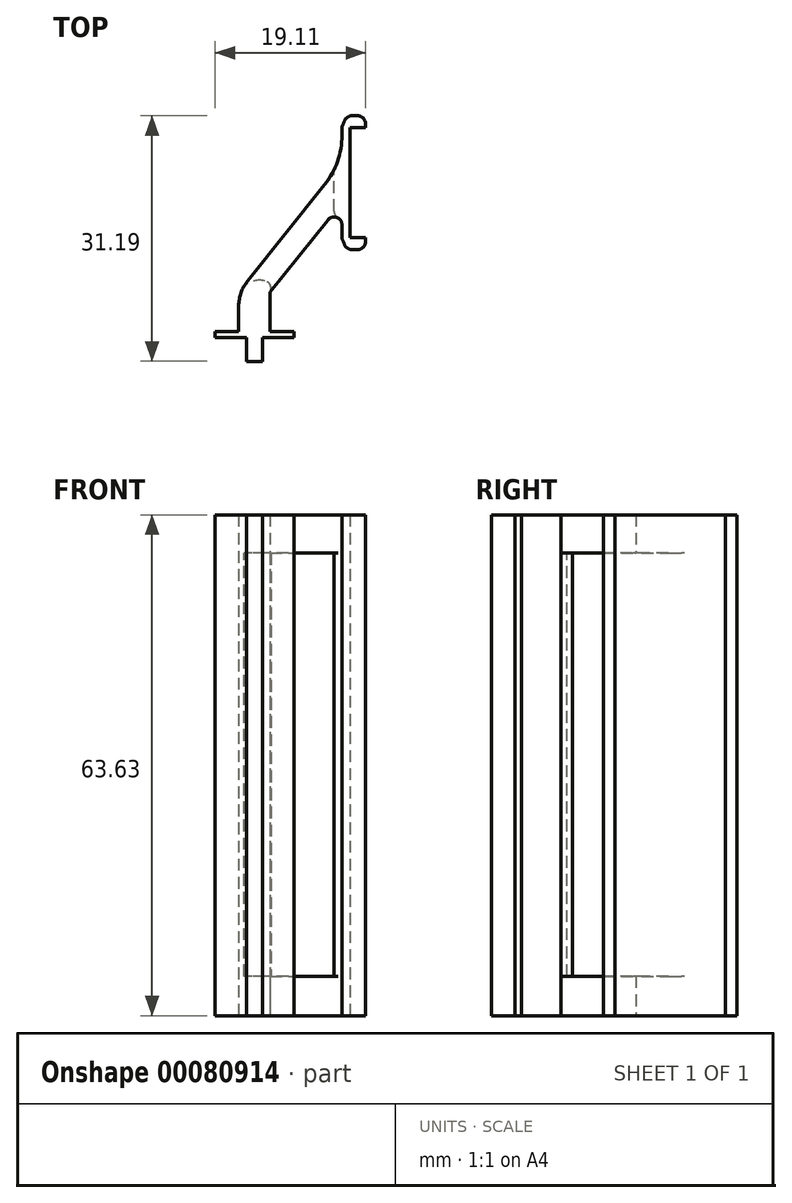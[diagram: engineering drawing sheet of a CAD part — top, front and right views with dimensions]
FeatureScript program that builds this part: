
annotation { "Feature Type Name" : "Feature", "Feature Type Description" : "" }
export const myFeature = defineFeature(function(context is Context, id is Id, definition is map)
    precondition{}
    {
        {
            var Q0;
            Q0=qCreatedBy(makeId("Top.planeOp"),FACE);
            var sketch = newSketch(context, id + "F0", { "sketchPlane" : qUnion([Q0])});
            skLineSegment(sketch, "E0.bottom", {"start": v(-4.08, -12.53) * mm, "end": v(-8.08, -12.53) * mm});
            skLineSegment(sketch, "E0.top", {"start": v(-4.08, -7.53) * mm, "end": v(-8.08, -7.53) * mm});
            skLineSegment(sketch, "E0.left", {"start": v(-4.08, -12.53) * mm, "end": v(-4.08, -7.53) * mm});
            skLineSegment(sketch, "E0.right", {"start": v(-8.08, -12.53) * mm, "end": v(-8.08, -7.53) * mm});
            skPoint(sketch, "E0.middle", {"position": v(-6.08, -10.03) * mm});
            skLineSegment(sketch, "E1", {"start": v(5.03, 8.86) * mm, "end": v(-8.08, -7.53) * mm});
            skLineSegment(sketch, "E2", {"start": v(5.03, 8.86) * mm, "end": v(5.03, 3.86) * mm});
            skLineSegment(sketch, "E3", {"start": v(-4.08, -7.53) * mm, "end": v(5.03, 3.86) * mm});
            skLineSegment(sketch, "E4.bottom", {"start": v(6.03, -1.14) * mm, "end": v(5.03, -1.14) * mm});
            skLineSegment(sketch, "E4.top", {"start": v(6.03, 13.86) * mm, "end": v(5.03, 13.86) * mm});
            skLineSegment(sketch, "E4.left", {"start": v(6.03, -1.14) * mm, "end": v(6.03, 13.86) * mm});
            skLineSegment(sketch, "E4.right", {"start": v(5.03, -1.14) * mm, "end": v(5.03, 13.86) * mm});
            skPoint(sketch, "E4.middle", {"position": v(5.53, 6.36) * mm});
            skLineSegment(sketch, "E5", {"start": v(5.03, 6.36) * mm, "end": v(12.44, 6.36) * mm});
            skLineSegment(sketch, "E6.bottom", {"start": v(6.03, -1.14) * mm, "end": v(8.03, -1.14) * mm});
            skLineSegment(sketch, "E6.top", {"start": v(6.03, -0.64) * mm, "end": v(8.03, -0.64) * mm});
            skLineSegment(sketch, "E6.left", {"start": v(6.03, -1.14) * mm, "end": v(6.03, -0.64) * mm});
            skLineSegment(sketch, "E6.right", {"start": v(8.03, -1.14) * mm, "end": v(8.03, -0.64) * mm});
            skLineSegment(sketch, "E7.bottom", {"start": v(6.03, 13.86) * mm, "end": v(8.03, 13.86) * mm});
            skLineSegment(sketch, "E7.top", {"start": v(6.03, 13.36) * mm, "end": v(8.03, 13.36) * mm});
            skLineSegment(sketch, "E7.left", {"start": v(6.03, 13.86) * mm, "end": v(6.03, 13.36) * mm});
            skLineSegment(sketch, "E7.right", {"start": v(8.03, 13.86) * mm, "end": v(8.03, 13.36) * mm});
            skLineSegment(sketch, "E8.bottom", {"start": v(8.03, 13.36) * mm, "end": v(7.03, 13.36) * mm});
            skLineSegment(sketch, "E8.top", {"start": v(8.03, 10.86) * mm, "end": v(7.03, 10.86) * mm});
            skLineSegment(sketch, "E8.left", {"start": v(8.03, 13.36) * mm, "end": v(8.03, 10.86) * mm});
            skLineSegment(sketch, "E8.right", {"start": v(7.03, 13.36) * mm, "end": v(7.03, 10.86) * mm});
            skLineSegment(sketch, "E9.bottom", {"start": v(8.03, -0.64) * mm, "end": v(7.03, -0.64) * mm});
            skLineSegment(sketch, "E9.top", {"start": v(8.03, 1.86) * mm, "end": v(7.03, 1.86) * mm});
            skLineSegment(sketch, "E9.left", {"start": v(8.03, -0.64) * mm, "end": v(8.03, 1.86) * mm});
            skLineSegment(sketch, "E9.right", {"start": v(7.03, -0.64) * mm, "end": v(7.03, 1.86) * mm});
            skLineSegment(sketch, "E10", {"start": v(-6.08, -10.03) * mm, "end": v(-6.08, -14.83) * mm});
            skLineSegment(sketch, "E11.bottom", {"start": v(-1.08, -13.33) * mm, "end": v(-11.08, -13.33) * mm});
            skLineSegment(sketch, "E11.top", {"start": v(-1.08, -12.53) * mm, "end": v(-11.08, -12.53) * mm});
            skLineSegment(sketch, "E11.left", {"start": v(-1.08, -13.33) * mm, "end": v(-1.08, -12.53) * mm});
            skLineSegment(sketch, "E11.right", {"start": v(-11.08, -13.33) * mm, "end": v(-11.08, -12.53) * mm});
            skPoint(sketch, "E11.middle", {"position": v(-6.08, -12.93) * mm});
            skLineSegment(sketch, "E12.bottom", {"start": v(-5.08, -16.33) * mm, "end": v(-7.08, -16.33) * mm});
            skLineSegment(sketch, "E12.top", {"start": v(-5.08, -13.33) * mm, "end": v(-7.08, -13.33) * mm});
            skLineSegment(sketch, "E12.left", {"start": v(-5.08, -16.33) * mm, "end": v(-5.08, -13.33) * mm});
            skLineSegment(sketch, "E12.right", {"start": v(-7.08, -16.33) * mm, "end": v(-7.08, -13.33) * mm});
            skPoint(sketch, "E12.middle", {"position": v(-6.08, -14.83) * mm});
            skLineSegment(sketch, "E13", {"start": v(4.1, 2.69) * mm, "end": v(4.1, 7.69) * mm});
            skLineSegment(sketch, "E14", {"start": v(-3.15, -6.36) * mm, "end": v(-3.15, -1.36) * mm});
            skSolve(sketch);
        }
        {
            var Q0;
            Q0=makeQuery(id+"F0.imprint","IMPRINT",FACE,{"disambiguationData":[TD([[makeQuery(id+"F0.imprint","IMPRINT",EDGE,{"derivedFrom":sQuery(id+"F0.wireOp",EDGE,"E0.top")}),1.0]])]});
            var Q1;
            {var subQ0=sQuery(id+"F0.wireOp",EDGE,"E0.top");Q1=makeQuery(id+"F0.imprint","IMPRINT",FACE,{"disambiguationData":[TD([[makeQuery(id+"F0.imprint","IMPRINT",EDGE,{"derivedFrom":subQ0}),-1.0]])]});}
            var Q2;
            {var subQ0=sQuery(id+"F0.wireOp",EDGE,"E13");Q2=makeQuery(id+"F0.imprint","IMPRINT",FACE,{"disambiguationData":[TD([[makeQuery(id+"F0.imprint","IMPRINT",EDGE,{"derivedFrom":subQ0}),1.0]])]});}
            var Q3;
            {var subQ6=sQuery(id+"F0.wireOp",EDGE,"E13");Q3=makeQuery(id+"F0.imprint","IMPRINT",FACE,{"disambiguationData":[TD([[makeQuery(id+"F0.imprint","IMPRINT",EDGE,{"derivedFrom":subQ6}),-1.0]])]});}
            var Q4;
            {var subQ4=sQuery(id+"F0.wireOp",EDGE,"E4.bottom");Q4=makeQuery(id+"F0.imprint","IMPRINT",FACE,{"disambiguationData":[TD([[makeQuery(id+"F0.imprint","IMPRINT",EDGE,{"derivedFrom":subQ4}),-1.0]])]});}
            var Q5;
            {var subQ2=sQuery(id+"F0.wireOp",EDGE,"E4.top");Q5=makeQuery(id+"F0.imprint","IMPRINT",FACE,{"disambiguationData":[TD([[makeQuery(id+"F0.imprint","IMPRINT",EDGE,{"derivedFrom":subQ2}),1.0]])]});}
            var Q6;
            Q6=makeQuery(id+"F0.imprint","IMPRINT",FACE,{"disambiguationData":[TD([[makeQuery(id+"F0.imprint","IMPRINT",EDGE,{"derivedFrom":sQuery(id+"F0.wireOp",EDGE,"E8.bottom")}),1.0]])]});
            var Q7;
            Q7=makeQuery(id+"F0.imprint","IMPRINT",FACE,{"disambiguationData":[TD([[makeQuery(id+"F0.imprint","IMPRINT",EDGE,{"derivedFrom":sQuery(id+"F0.wireOp",EDGE,"E7.bottom")}),-1.0]])]});
            var Q8;
            Q8=makeQuery(id+"F0.imprint","IMPRINT",FACE,{"disambiguationData":[TD([[makeQuery(id+"F0.imprint","IMPRINT",EDGE,{"derivedFrom":sQuery(id+"F0.wireOp",EDGE,"E9.bottom")}),-1.0]])]});
            var Q9;
            Q9=makeQuery(id+"F0.imprint","IMPRINT",FACE,{"disambiguationData":[TD([[makeQuery(id+"F0.imprint","IMPRINT",EDGE,{"derivedFrom":sQuery(id+"F0.wireOp",EDGE,"E6.bottom")}),1.0]])]});
            var Q10;
            {var subQ4=sQuery(id+"F0.wireOp",EDGE,"E11.left");Q10=makeQuery(id+"F0.imprint","IMPRINT",FACE,{"disambiguationData":[TD([[makeQuery(id+"F0.imprint","IMPRINT",EDGE,{"derivedFrom":subQ4}),1.0]])]});}
            var Q11;
            {var subQ2=sQuery(id+"F0.wireOp",EDGE,"E11.right");Q11=makeQuery(id+"F0.imprint","IMPRINT",FACE,{"disambiguationData":[TD([[makeQuery(id+"F0.imprint","IMPRINT",EDGE,{"derivedFrom":subQ2}),-1.0]])]});}
            var Q12;
            Q12=makeQuery(id+"F0.imprint","IMPRINT",FACE,{"disambiguationData":[TD([[makeQuery(id+"F0.imprint","IMPRINT",EDGE,{"derivedFrom":sQuery(id+"F0.wireOp",EDGE,"E12.bottom")}),-1.0]])]});
            extrude(context, id + "F1", {"entities" : qUnion([Q0, Q1, Q2, Q3, Q4, Q5, Q6, Q7, Q8, Q9, Q10, Q11, Q12]), "depth" : 240 * mm});
        }
        {
            var Q0;
            Q0=makeQuery(id+"F1.opExtrude","SWEPT_FACE",FACE,{"disambiguationData":[OSD([sQuery(id+"F0.wireOp",EDGE,"E4.top"),sQuery(id+"F0.wireOp",EDGE,"E7.bottom")])]});
            var sketch = newSketch(context, id + "F2", { "sketchPlane" : qUnion([Q0])});
            skLineSegment(sketch, "E15", {"start": v(3.47, 0) * mm, "end": v(3.47, 246.31) * mm});
            skLineSegment(sketch, "E16", {"start": v(-4.03, 0) * mm, "end": v(-4.03, 246.65) * mm});
            skLineSegment(sketch, "E17", {"start": v(19.34, 240) * mm, "end": v(-16.18, 240) * mm});
            skLineSegment(sketch, "E18", {"start": v(17.67, 0) * mm, "end": v(-15.98, 0) * mm});
            skLineSegment(sketch, "E19", {"start": v(3.47, 5) * mm, "end": v(-4.03, 5) * mm});
            skLineSegment(sketch, "E20", {"start": v(3.47, 58.75) * mm, "end": v(-4.03, 58.75) * mm});
            skLineSegment(sketch, "E21", {"start": v(3.47, 63.75) * mm, "end": v(-4.03, 63.75) * mm});
            skLineSegment(sketch, "E22", {"start": v(3.47, 117.5) * mm, "end": v(-4.03, 117.5) * mm});
            skLineSegment(sketch, "E23", {"start": v(3.47, 122.5) * mm, "end": v(-4.03, 122.5) * mm});
            skLineSegment(sketch, "E24", {"start": v(3.47, 176.25) * mm, "end": v(-4.03, 176.25) * mm});
            skLineSegment(sketch, "E25", {"start": v(3.47, 181.25) * mm, "end": v(-4.03, 181.25) * mm});
            skLineSegment(sketch, "E26", {"start": v(3.47, 235) * mm, "end": v(-4.03, 235) * mm});
            skSolve(sketch);
        }
        {
            var Q0;
            {var subQ0=sQuery(id+"F2.wireOp",EDGE,"E25");Q0=makeQuery(id+"F2.imprint","IMPRINT",FACE,{"disambiguationData":[TD([[makeQuery(id+"F2.imprint","IMPRINT",EDGE,{"derivedFrom":subQ0}),-1.0]])]});}
            var Q1;
            {var subQ0=sQuery(id+"F2.wireOp",EDGE,"E23");Q1=makeQuery(id+"F2.imprint","IMPRINT",FACE,{"disambiguationData":[TD([[makeQuery(id+"F2.imprint","IMPRINT",EDGE,{"derivedFrom":subQ0}),-1.0]])]});}
            var Q2;
            {var subQ0=sQuery(id+"F2.wireOp",EDGE,"E21");Q2=makeQuery(id+"F2.imprint","IMPRINT",FACE,{"disambiguationData":[TD([[makeQuery(id+"F2.imprint","IMPRINT",EDGE,{"derivedFrom":subQ0}),-1.0]])]});}
            var Q3;
            {var subQ0=sQuery(id+"F2.wireOp",EDGE,"E19");Q3=makeQuery(id+"F2.imprint","IMPRINT",FACE,{"disambiguationData":[TD([[makeQuery(id+"F2.imprint","IMPRINT",EDGE,{"derivedFrom":subQ0}),-1.0]])]});}
            extrude(context, id + "F3", {"entities" : qUnion([Q0, Q1, Q2, Q3]), "operationType" : NewBodyOperationType.REMOVE, "oppositeDirection" : true, "depth" : 25 * mm});
        }
        {
            var Q0;
            Q0=makeQuery(id+"F1.opExtrude","SWEPT_EDGE",EDGE,{"disambiguationData":[OSD([sQuery(id+"F0.wireOp",EDGE,"E3"),sQuery(id+"F0.wireOp",EDGE,"E4.right")])]});
            fillet(context, id + "F4", {"entities" : qUnion([Q0]), "radius" : 1 * mm, "tangentPropagation" : true, "allowEdgeOverflow" : false});
        }
        {
            var Q0;
            Q0=makeQuery(id+"F1.opExtrude","SWEPT_EDGE",EDGE,{"disambiguationData":[OSD([sQuery(id+"F0.wireOp",EDGE,"E1"),sQuery(id+"F0.wireOp",EDGE,"E4.right")])]});
            fillet(context, id + "F5", {"entities" : qUnion([Q0]), "radius" : 10 * mm, "tangentPropagation" : true, "allowEdgeOverflow" : false});
        }
        {
            var Q0;
            Q0=makeQuery(id+"F1.opExtrude","SWEPT_EDGE",EDGE,{"disambiguationData":[OSD([sQuery(id+"F0.wireOp",EDGE,"E4.bottom"),sQuery(id+"F0.wireOp",EDGE,"E4.right")])]});
            var Q1;
            Q1=makeQuery(id+"F1.opExtrude","SWEPT_EDGE",EDGE,{"disambiguationData":[OSD([sQuery(id+"F0.wireOp",EDGE,"E4.top"),sQuery(id+"F0.wireOp",EDGE,"E4.right")])]});
            fillet(context, id + "F6", {"entities" : qUnion([Q0, Q1]), "radius" : .5 * mm, "tangentPropagation" : true, "allowEdgeOverflow" : false});
        }
        {
            var Q0;
            {var subQ0=sQuery(id+"F2.wireOp",EDGE,"E15");Q0=makeQuery(id+"F3.boolean.opBoolean","INTERSECT",EDGE,{"derivedFrom":[makeQuery(id+"F1.opExtrude","SWEPT_FACE",FACE,{"disambiguationData":[OSD([sQuery(id+"F0.wireOp",EDGE,"E1")])]}),makeQuery(id+"F3.opExtrude","SWEPT_FACE",FACE,{"disambiguationData":[OSD([subQ0]),TDD([makeQuery(id+"F2.imprint","IMPRINT",EDGE,{"disambiguationData":[TD([[makeQuery(id+"F2.imprint","INTERSECT",VERTEX,{"derivedFrom":[subQ0,sQuery(id+"F2.wireOp",EDGE,"E25")]}),-1.0]])],"derivedFrom":subQ0})])]})]});}
            var Q1;
            {var subQ0=sQuery(id+"F2.wireOp",EDGE,"E15");Q1=makeQuery(id+"F3.boolean.opBoolean","INTERSECT",EDGE,{"derivedFrom":[makeQuery(id+"F1.opExtrude","SWEPT_FACE",FACE,{"disambiguationData":[OSD([sQuery(id+"F0.wireOp",EDGE,"E1")])]}),makeQuery(id+"F3.opExtrude","SWEPT_FACE",FACE,{"disambiguationData":[OSD([subQ0]),TDD([makeQuery(id+"F2.imprint","IMPRINT",EDGE,{"disambiguationData":[TD([[makeQuery(id+"F2.imprint","INTERSECT",VERTEX,{"derivedFrom":[subQ0,sQuery(id+"F2.wireOp",EDGE,"E23")]}),-1.0]])],"derivedFrom":subQ0})])]})]});}
            var Q2;
            {var subQ0=sQuery(id+"F2.wireOp",EDGE,"E15");Q2=makeQuery(id+"F3.boolean.opBoolean","INTERSECT",EDGE,{"derivedFrom":[makeQuery(id+"F1.opExtrude","SWEPT_FACE",FACE,{"disambiguationData":[OSD([sQuery(id+"F0.wireOp",EDGE,"E1")])]}),makeQuery(id+"F3.opExtrude","SWEPT_FACE",FACE,{"disambiguationData":[OSD([subQ0]),TDD([makeQuery(id+"F2.imprint","IMPRINT",EDGE,{"disambiguationData":[TD([[makeQuery(id+"F2.imprint","INTERSECT",VERTEX,{"derivedFrom":[subQ0,sQuery(id+"F2.wireOp",EDGE,"E21")]}),-1.0]])],"derivedFrom":subQ0})])]})]});}
            var Q3;
            {var subQ0=sQuery(id+"F2.wireOp",EDGE,"E15");Q3=makeQuery(id+"F3.boolean.opBoolean","INTERSECT",EDGE,{"derivedFrom":[makeQuery(id+"F1.opExtrude","SWEPT_FACE",FACE,{"disambiguationData":[OSD([sQuery(id+"F0.wireOp",EDGE,"E1")])]}),makeQuery(id+"F3.opExtrude","SWEPT_FACE",FACE,{"disambiguationData":[OSD([subQ0]),TDD([makeQuery(id+"F2.imprint","IMPRINT",EDGE,{"disambiguationData":[TD([[makeQuery(id+"F2.imprint","INTERSECT",VERTEX,{"derivedFrom":[subQ0,sQuery(id+"F2.wireOp",EDGE,"E19")]}),-1.0]])],"derivedFrom":subQ0})])]})]});}
            fillet(context, id + "F7", {"entities" : qUnion([Q0, Q1, Q2, Q3]), "radius" : 3 * mm, "tangentPropagation" : true, "allowEdgeOverflow" : false});
        }
        {
            var Q0;
            {var subQ0=sQuery(id+"F2.wireOp",EDGE,"E16");Q0=makeQuery(id+"F4.opFillet","BLEND_EDGE",EDGE,{"blendedFrom":[makeQuery(id+"F1.opExtrude","SWEPT_EDGE",EDGE,{"disambiguationData":[OSD([sQuery(id+"F0.wireOp",EDGE,"E3"),sQuery(id+"F0.wireOp",EDGE,"E4.right")])]}),makeQuery(id+"F3.boolean.opBoolean","COPY",FACE,{"derivedFrom":makeQuery(id+"F3.opExtrude","SWEPT_FACE",FACE,{"disambiguationData":[OSD([subQ0]),TDD([makeQuery(id+"F2.imprint","IMPRINT",EDGE,{"disambiguationData":[TD([[makeQuery(id+"F2.imprint","INTERSECT",VERTEX,{"derivedFrom":[subQ0,sQuery(id+"F2.wireOp",EDGE,"E25")]}),-1.0]])],"derivedFrom":subQ0})])]})})],"blendedInto":[makeQuery(id+"F3.boolean.opBoolean","COPY",FACE,{"derivedFrom":makeQuery(id+"F3.opExtrude","SWEPT_FACE",FACE,{"disambiguationData":[OSD([subQ0]),TDD([makeQuery(id+"F2.imprint","IMPRINT",EDGE,{"disambiguationData":[TD([[makeQuery(id+"F2.imprint","INTERSECT",VERTEX,{"derivedFrom":[subQ0,sQuery(id+"F2.wireOp",EDGE,"E25")]}),-1.0]])],"derivedFrom":subQ0})])]})})]});}
            var Q1;
            {var subQ0=sQuery(id+"F2.wireOp",EDGE,"E16");Q1=makeQuery(id+"F5.opFillet","BLEND_EDGE",EDGE,{"blendedFrom":[makeQuery(id+"F1.opExtrude","SWEPT_EDGE",EDGE,{"disambiguationData":[OSD([sQuery(id+"F0.wireOp",EDGE,"E1"),sQuery(id+"F0.wireOp",EDGE,"E4.right")])]}),makeQuery(id+"F3.boolean.opBoolean","COPY",FACE,{"derivedFrom":makeQuery(id+"F3.opExtrude","SWEPT_FACE",FACE,{"disambiguationData":[OSD([subQ0]),TDD([makeQuery(id+"F2.imprint","IMPRINT",EDGE,{"disambiguationData":[TD([[makeQuery(id+"F2.imprint","INTERSECT",VERTEX,{"derivedFrom":[subQ0,sQuery(id+"F2.wireOp",EDGE,"E25")]}),-1.0]])],"derivedFrom":subQ0})])]})})],"blendedInto":[makeQuery(id+"F3.boolean.opBoolean","COPY",FACE,{"derivedFrom":makeQuery(id+"F3.opExtrude","SWEPT_FACE",FACE,{"disambiguationData":[OSD([subQ0]),TDD([makeQuery(id+"F2.imprint","IMPRINT",EDGE,{"disambiguationData":[TD([[makeQuery(id+"F2.imprint","INTERSECT",VERTEX,{"derivedFrom":[subQ0,sQuery(id+"F2.wireOp",EDGE,"E25")]}),-1.0]])],"derivedFrom":subQ0})])]})})]});}
            var Q2;
            {var subQ0=sQuery(id+"F2.wireOp",EDGE,"E16");Q2=makeQuery(id+"F5.opFillet","BLEND_EDGE",EDGE,{"blendedFrom":[makeQuery(id+"F1.opExtrude","SWEPT_EDGE",EDGE,{"disambiguationData":[OSD([sQuery(id+"F0.wireOp",EDGE,"E1"),sQuery(id+"F0.wireOp",EDGE,"E4.right")])]}),makeQuery(id+"F3.boolean.opBoolean","COPY",FACE,{"derivedFrom":makeQuery(id+"F3.opExtrude","SWEPT_FACE",FACE,{"disambiguationData":[OSD([subQ0]),TDD([makeQuery(id+"F2.imprint","IMPRINT",EDGE,{"disambiguationData":[TD([[makeQuery(id+"F2.imprint","INTERSECT",VERTEX,{"derivedFrom":[subQ0,sQuery(id+"F2.wireOp",EDGE,"E23")]}),-1.0]])],"derivedFrom":subQ0})])]})})],"blendedInto":[makeQuery(id+"F3.boolean.opBoolean","COPY",FACE,{"derivedFrom":makeQuery(id+"F3.opExtrude","SWEPT_FACE",FACE,{"disambiguationData":[OSD([subQ0]),TDD([makeQuery(id+"F2.imprint","IMPRINT",EDGE,{"disambiguationData":[TD([[makeQuery(id+"F2.imprint","INTERSECT",VERTEX,{"derivedFrom":[subQ0,sQuery(id+"F2.wireOp",EDGE,"E23")]}),-1.0]])],"derivedFrom":subQ0})])]})})]});}
            var Q3;
            {var subQ0=sQuery(id+"F2.wireOp",EDGE,"E16");Q3=makeQuery(id+"F4.opFillet","BLEND_EDGE",EDGE,{"blendedFrom":[makeQuery(id+"F1.opExtrude","SWEPT_EDGE",EDGE,{"disambiguationData":[OSD([sQuery(id+"F0.wireOp",EDGE,"E3"),sQuery(id+"F0.wireOp",EDGE,"E4.right")])]}),makeQuery(id+"F3.boolean.opBoolean","COPY",FACE,{"derivedFrom":makeQuery(id+"F3.opExtrude","SWEPT_FACE",FACE,{"disambiguationData":[OSD([subQ0]),TDD([makeQuery(id+"F2.imprint","IMPRINT",EDGE,{"disambiguationData":[TD([[makeQuery(id+"F2.imprint","INTERSECT",VERTEX,{"derivedFrom":[subQ0,sQuery(id+"F2.wireOp",EDGE,"E23")]}),-1.0]])],"derivedFrom":subQ0})])]})})],"blendedInto":[makeQuery(id+"F3.boolean.opBoolean","COPY",FACE,{"derivedFrom":makeQuery(id+"F3.opExtrude","SWEPT_FACE",FACE,{"disambiguationData":[OSD([subQ0]),TDD([makeQuery(id+"F2.imprint","IMPRINT",EDGE,{"disambiguationData":[TD([[makeQuery(id+"F2.imprint","INTERSECT",VERTEX,{"derivedFrom":[subQ0,sQuery(id+"F2.wireOp",EDGE,"E23")]}),-1.0]])],"derivedFrom":subQ0})])]})})]});}
            var Q4;
            {var subQ0=sQuery(id+"F2.wireOp",EDGE,"E16");Q4=makeQuery(id+"F4.opFillet","BLEND_EDGE",EDGE,{"blendedFrom":[makeQuery(id+"F1.opExtrude","SWEPT_EDGE",EDGE,{"disambiguationData":[OSD([sQuery(id+"F0.wireOp",EDGE,"E3"),sQuery(id+"F0.wireOp",EDGE,"E4.right")])]}),makeQuery(id+"F3.boolean.opBoolean","COPY",FACE,{"derivedFrom":makeQuery(id+"F3.opExtrude","SWEPT_FACE",FACE,{"disambiguationData":[OSD([subQ0]),TDD([makeQuery(id+"F2.imprint","IMPRINT",EDGE,{"disambiguationData":[TD([[makeQuery(id+"F2.imprint","INTERSECT",VERTEX,{"derivedFrom":[subQ0,sQuery(id+"F2.wireOp",EDGE,"E21")]}),-1.0]])],"derivedFrom":subQ0})])]})})],"blendedInto":[makeQuery(id+"F3.boolean.opBoolean","COPY",FACE,{"derivedFrom":makeQuery(id+"F3.opExtrude","SWEPT_FACE",FACE,{"disambiguationData":[OSD([subQ0]),TDD([makeQuery(id+"F2.imprint","IMPRINT",EDGE,{"disambiguationData":[TD([[makeQuery(id+"F2.imprint","INTERSECT",VERTEX,{"derivedFrom":[subQ0,sQuery(id+"F2.wireOp",EDGE,"E21")]}),-1.0]])],"derivedFrom":subQ0})])]})})]});}
            var Q5;
            {var subQ0=sQuery(id+"F2.wireOp",EDGE,"E16");Q5=makeQuery(id+"F5.opFillet","BLEND_EDGE",EDGE,{"blendedFrom":[makeQuery(id+"F1.opExtrude","SWEPT_EDGE",EDGE,{"disambiguationData":[OSD([sQuery(id+"F0.wireOp",EDGE,"E1"),sQuery(id+"F0.wireOp",EDGE,"E4.right")])]}),makeQuery(id+"F3.boolean.opBoolean","COPY",FACE,{"derivedFrom":makeQuery(id+"F3.opExtrude","SWEPT_FACE",FACE,{"disambiguationData":[OSD([subQ0]),TDD([makeQuery(id+"F2.imprint","IMPRINT",EDGE,{"disambiguationData":[TD([[makeQuery(id+"F2.imprint","INTERSECT",VERTEX,{"derivedFrom":[subQ0,sQuery(id+"F2.wireOp",EDGE,"E21")]}),-1.0]])],"derivedFrom":subQ0})])]})})],"blendedInto":[makeQuery(id+"F3.boolean.opBoolean","COPY",FACE,{"derivedFrom":makeQuery(id+"F3.opExtrude","SWEPT_FACE",FACE,{"disambiguationData":[OSD([subQ0]),TDD([makeQuery(id+"F2.imprint","IMPRINT",EDGE,{"disambiguationData":[TD([[makeQuery(id+"F2.imprint","INTERSECT",VERTEX,{"derivedFrom":[subQ0,sQuery(id+"F2.wireOp",EDGE,"E21")]}),-1.0]])],"derivedFrom":subQ0})])]})})]});}
            var Q6;
            {var subQ0=sQuery(id+"F2.wireOp",EDGE,"E16");Q6=makeQuery(id+"F4.opFillet","BLEND_EDGE",EDGE,{"blendedFrom":[makeQuery(id+"F1.opExtrude","SWEPT_EDGE",EDGE,{"disambiguationData":[OSD([sQuery(id+"F0.wireOp",EDGE,"E3"),sQuery(id+"F0.wireOp",EDGE,"E4.right")])]}),makeQuery(id+"F3.boolean.opBoolean","COPY",FACE,{"derivedFrom":makeQuery(id+"F3.opExtrude","SWEPT_FACE",FACE,{"disambiguationData":[OSD([subQ0]),TDD([makeQuery(id+"F2.imprint","IMPRINT",EDGE,{"disambiguationData":[TD([[makeQuery(id+"F2.imprint","INTERSECT",VERTEX,{"derivedFrom":[subQ0,sQuery(id+"F2.wireOp",EDGE,"E19")]}),-1.0]])],"derivedFrom":subQ0})])]})})],"blendedInto":[makeQuery(id+"F3.boolean.opBoolean","COPY",FACE,{"derivedFrom":makeQuery(id+"F3.opExtrude","SWEPT_FACE",FACE,{"disambiguationData":[OSD([subQ0]),TDD([makeQuery(id+"F2.imprint","IMPRINT",EDGE,{"disambiguationData":[TD([[makeQuery(id+"F2.imprint","INTERSECT",VERTEX,{"derivedFrom":[subQ0,sQuery(id+"F2.wireOp",EDGE,"E19")]}),-1.0]])],"derivedFrom":subQ0})])]})})]});}
            var Q7;
            {var subQ0=sQuery(id+"F2.wireOp",EDGE,"E16");Q7=makeQuery(id+"F5.opFillet","BLEND_EDGE",EDGE,{"blendedFrom":[makeQuery(id+"F1.opExtrude","SWEPT_EDGE",EDGE,{"disambiguationData":[OSD([sQuery(id+"F0.wireOp",EDGE,"E1"),sQuery(id+"F0.wireOp",EDGE,"E4.right")])]}),makeQuery(id+"F3.boolean.opBoolean","COPY",FACE,{"derivedFrom":makeQuery(id+"F3.opExtrude","SWEPT_FACE",FACE,{"disambiguationData":[OSD([subQ0]),TDD([makeQuery(id+"F2.imprint","IMPRINT",EDGE,{"disambiguationData":[TD([[makeQuery(id+"F2.imprint","INTERSECT",VERTEX,{"derivedFrom":[subQ0,sQuery(id+"F2.wireOp",EDGE,"E19")]}),-1.0]])],"derivedFrom":subQ0})])]})})],"blendedInto":[makeQuery(id+"F3.boolean.opBoolean","COPY",FACE,{"derivedFrom":makeQuery(id+"F3.opExtrude","SWEPT_FACE",FACE,{"disambiguationData":[OSD([subQ0]),TDD([makeQuery(id+"F2.imprint","IMPRINT",EDGE,{"disambiguationData":[TD([[makeQuery(id+"F2.imprint","INTERSECT",VERTEX,{"derivedFrom":[subQ0,sQuery(id+"F2.wireOp",EDGE,"E19")]}),-1.0]])],"derivedFrom":subQ0})])]})})]});}
            fillet(context, id + "F8", {"entities" : qUnion([Q0, Q1, Q2, Q3, Q4, Q5, Q6, Q7]), "radius" : 1 * mm, "tangentPropagation" : true, "allowEdgeOverflow" : false});
        }
        {
            var Q0;
            {var subQ0=sQuery(id+"F2.wireOp",EDGE,"E15");Q0=makeQuery(id+"F7.opFillet","BLEND_EDGE",EDGE,{"blendedFrom":[makeQuery(id+"F3.boolean.opBoolean","INTERSECT",EDGE,{"derivedFrom":[makeQuery(id+"F1.opExtrude","SWEPT_FACE",FACE,{"disambiguationData":[OSD([sQuery(id+"F0.wireOp",EDGE,"E1")])]}),makeQuery(id+"F3.opExtrude","SWEPT_FACE",FACE,{"disambiguationData":[OSD([subQ0]),TDD([makeQuery(id+"F2.imprint","IMPRINT",EDGE,{"disambiguationData":[TD([[makeQuery(id+"F2.imprint","INTERSECT",VERTEX,{"derivedFrom":[subQ0,sQuery(id+"F2.wireOp",EDGE,"E25")]}),-1.0]])],"derivedFrom":subQ0})])]})]}),makeQuery(id+"F1.opExtrude","SWEPT_FACE",FACE,{"disambiguationData":[OSD([sQuery(id+"F0.wireOp",EDGE,"E3")])]})],"blendedInto":[makeQuery(id+"F1.opExtrude","SWEPT_FACE",FACE,{"disambiguationData":[OSD([sQuery(id+"F0.wireOp",EDGE,"E3")])]})]});}
            var Q1;
            {var subQ0=sQuery(id+"F2.wireOp",EDGE,"E15");Q1=makeQuery(id+"F7.opFillet","BLEND_EDGE",EDGE,{"blendedFrom":[makeQuery(id+"F3.boolean.opBoolean","INTERSECT",EDGE,{"derivedFrom":[makeQuery(id+"F1.opExtrude","SWEPT_FACE",FACE,{"disambiguationData":[OSD([sQuery(id+"F0.wireOp",EDGE,"E1")])]}),makeQuery(id+"F3.opExtrude","SWEPT_FACE",FACE,{"disambiguationData":[OSD([subQ0]),TDD([makeQuery(id+"F2.imprint","IMPRINT",EDGE,{"disambiguationData":[TD([[makeQuery(id+"F2.imprint","INTERSECT",VERTEX,{"derivedFrom":[subQ0,sQuery(id+"F2.wireOp",EDGE,"E23")]}),-1.0]])],"derivedFrom":subQ0})])]})]}),makeQuery(id+"F1.opExtrude","SWEPT_FACE",FACE,{"disambiguationData":[OSD([sQuery(id+"F0.wireOp",EDGE,"E3")])]})],"blendedInto":[makeQuery(id+"F1.opExtrude","SWEPT_FACE",FACE,{"disambiguationData":[OSD([sQuery(id+"F0.wireOp",EDGE,"E3")])]})]});}
            var Q2;
            {var subQ0=sQuery(id+"F2.wireOp",EDGE,"E15");Q2=makeQuery(id+"F7.opFillet","BLEND_EDGE",EDGE,{"blendedFrom":[makeQuery(id+"F3.boolean.opBoolean","INTERSECT",EDGE,{"derivedFrom":[makeQuery(id+"F1.opExtrude","SWEPT_FACE",FACE,{"disambiguationData":[OSD([sQuery(id+"F0.wireOp",EDGE,"E1")])]}),makeQuery(id+"F3.opExtrude","SWEPT_FACE",FACE,{"disambiguationData":[OSD([subQ0]),TDD([makeQuery(id+"F2.imprint","IMPRINT",EDGE,{"disambiguationData":[TD([[makeQuery(id+"F2.imprint","INTERSECT",VERTEX,{"derivedFrom":[subQ0,sQuery(id+"F2.wireOp",EDGE,"E21")]}),-1.0]])],"derivedFrom":subQ0})])]})]}),makeQuery(id+"F1.opExtrude","SWEPT_FACE",FACE,{"disambiguationData":[OSD([sQuery(id+"F0.wireOp",EDGE,"E3")])]})],"blendedInto":[makeQuery(id+"F1.opExtrude","SWEPT_FACE",FACE,{"disambiguationData":[OSD([sQuery(id+"F0.wireOp",EDGE,"E3")])]})]});}
            var Q3;
            {var subQ0=sQuery(id+"F2.wireOp",EDGE,"E15");Q3=makeQuery(id+"F7.opFillet","BLEND_EDGE",EDGE,{"blendedFrom":[makeQuery(id+"F3.boolean.opBoolean","INTERSECT",EDGE,{"derivedFrom":[makeQuery(id+"F1.opExtrude","SWEPT_FACE",FACE,{"disambiguationData":[OSD([sQuery(id+"F0.wireOp",EDGE,"E1")])]}),makeQuery(id+"F3.opExtrude","SWEPT_FACE",FACE,{"disambiguationData":[OSD([subQ0]),TDD([makeQuery(id+"F2.imprint","IMPRINT",EDGE,{"disambiguationData":[TD([[makeQuery(id+"F2.imprint","INTERSECT",VERTEX,{"derivedFrom":[subQ0,sQuery(id+"F2.wireOp",EDGE,"E19")]}),-1.0]])],"derivedFrom":subQ0})])]})]}),makeQuery(id+"F1.opExtrude","SWEPT_FACE",FACE,{"disambiguationData":[OSD([sQuery(id+"F0.wireOp",EDGE,"E3")])]})],"blendedInto":[makeQuery(id+"F1.opExtrude","SWEPT_FACE",FACE,{"disambiguationData":[OSD([sQuery(id+"F0.wireOp",EDGE,"E3")])]})]});}
            fillet(context, id + "F9", {"entities" : qUnion([Q0, Q1, Q2, Q3]), "radius" : 1 * mm, "tangentPropagation" : true, "allowEdgeOverflow" : false});
        }
        {
            var Q0;
            Q0=makeQuery(id+"F1.opExtrude","SWEPT_EDGE",EDGE,{"disambiguationData":[OSD([sQuery(id+"F0.wireOp",EDGE,"E0.top"),sQuery(id+"F0.wireOp",EDGE,"E0.right"),sQuery(id+"F0.wireOp",EDGE,"E1")])]});
            fillet(context, id + "F10", {"entities" : qUnion([Q0]), "radius" : 5 * mm, "tangentPropagation" : true, "allowEdgeOverflow" : false});
        }
        {
            var Q0;
            Q0=qCreatedBy(makeId("Top.planeOp"),FACE);
            var sketch = newSketch(context, id + "F11", { "sketchPlane" : qUnion([Q0])});
            skLineSegment(sketch, "E27.bottom", {"start": v(30, -30) * mm, "end": v(-30, -30) * mm});
            skLineSegment(sketch, "E27.top", {"start": v(30, 30) * mm, "end": v(-30, 30) * mm});
            skLineSegment(sketch, "E27.left", {"start": v(30, -30) * mm, "end": v(30, 30) * mm});
            skLineSegment(sketch, "E27.right", {"start": v(-30, -30) * mm, "end": v(-30, 30) * mm});
            skPoint(sketch, "E27.middle", {"position": v(0, 0) * mm});
            skSolve(sketch);
        }
        {
            var Q0;
            Q0=makeQuery(id+"F1.opExtrude","CAP_FACE",FACE,{"disambiguationData":[OSD([sQuery(id+"F0.wireOp",EDGE,"E0.left"),sQuery(id+"F0.wireOp",EDGE,"E0.right"),sQuery(id+"F0.wireOp",EDGE,"E1"),sQuery(id+"F0.wireOp",EDGE,"E3"),sQuery(id+"F0.wireOp",EDGE,"E4.bottom"),sQuery(id+"F0.wireOp",EDGE,"E4.top"),sQuery(id+"F0.wireOp",EDGE,"E4.left"),sQuery(id+"F0.wireOp",EDGE,"E4.right"),sQuery(id+"F0.wireOp",EDGE,"E6.bottom"),sQuery(id+"F0.wireOp",EDGE,"E6.top"),sQuery(id+"F0.wireOp",EDGE,"E6.right"),sQuery(id+"F0.wireOp",EDGE,"E7.bottom"),sQuery(id+"F0.wireOp",EDGE,"E7.top"),sQuery(id+"F0.wireOp",EDGE,"E7.right"),sQuery(id+"F0.wireOp",EDGE,"E8.top"),sQuery(id+"F0.wireOp",EDGE,"E8.left"),sQuery(id+"F0.wireOp",EDGE,"E8.right"),sQuery(id+"F0.wireOp",EDGE,"E9.top"),sQuery(id+"F0.wireOp",EDGE,"E9.left"),sQuery(id+"F0.wireOp",EDGE,"E9.right"),sQuery(id+"F0.wireOp",EDGE,"E11.bottom"),sQuery(id+"F0.wireOp",EDGE,"E11.top"),sQuery(id+"F0.wireOp",EDGE,"E11.left"),sQuery(id+"F0.wireOp",EDGE,"E11.right"),sQuery(id+"F0.wireOp",EDGE,"E12.bottom"),sQuery(id+"F0.wireOp",EDGE,"E12.left"),sQuery(id+"F0.wireOp",EDGE,"E12.right")])],"isStart":false});
            extrude(context, id + "F12", {"entities" : qUnion([Q0]), "operationType" : NewBodyOperationType.REMOVE, "oppositeDirection" : true, "depth" : 176.37 * mm});
        }
        {
            var Q0;
            Q0=makeQuery(id+"F1.opExtrude","SWEPT_FACE",FACE,{"disambiguationData":[OSD([sQuery(id+"F0.wireOp",EDGE,"E4.top"),sQuery(id+"F0.wireOp",EDGE,"E7.bottom")])]});
            extrude(context, id + "F13", {"entities" : qUnion([Q0]), "operationType" : NewBodyOperationType.ADD, "depth" : 1 * mm});
        }
        {
            var Q0;
            Q0=makeQuery(id+"F1.opExtrude","SWEPT_FACE",FACE,{"disambiguationData":[OSD([sQuery(id+"F0.wireOp",EDGE,"E4.bottom"),sQuery(id+"F0.wireOp",EDGE,"E6.bottom")])]});
            extrude(context, id + "F14", {"entities" : qUnion([Q0]), "operationType" : NewBodyOperationType.ADD, "depth" : 1 * mm});
        }
        {
            var Q0;
            {var subQ0=sQuery(id+"F0.wireOp",EDGE,"E6.bottom");var subQ1=sQuery(id+"F0.wireOp",EDGE,"E4.right");var subQ2=sQuery(id+"F0.wireOp",EDGE,"E4.bottom");Q0=makeQuery(id+"F14.boolean.opBoolean","MERGE",EDGE,{"derivedFrom":[makeQuery(id+"F6.opFillet","BLEND_EDGE",EDGE,{"blendedFrom":[makeQuery(id+"F1.opExtrude","SWEPT_EDGE",EDGE,{"disambiguationData":[OSD([subQ2,subQ1])]}),makeQuery(id+"F1.opExtrude","SWEPT_FACE",FACE,{"disambiguationData":[OSD([subQ2,subQ0])]})],"blendedInto":[makeQuery(id+"F1.opExtrude","SWEPT_FACE",FACE,{"disambiguationData":[OSD([subQ2,subQ0])]})]}),makeQuery(id+"F14.opExtrude","CAP_EDGE",EDGE,{"disambiguationData":[OSD([subQ2,subQ1,subQ0])],"isStart":true})]});}
            var Q1;
            {var subQ0=sQuery(id+"F0.wireOp",EDGE,"E7.bottom");var subQ1=sQuery(id+"F0.wireOp",EDGE,"E4.right");var subQ2=sQuery(id+"F0.wireOp",EDGE,"E4.top");Q1=makeQuery(id+"F13.boolean.opBoolean","MERGE",EDGE,{"derivedFrom":[makeQuery(id+"F6.opFillet","BLEND_EDGE",EDGE,{"blendedFrom":[makeQuery(id+"F1.opExtrude","SWEPT_EDGE",EDGE,{"disambiguationData":[OSD([subQ2,subQ1])]}),makeQuery(id+"F1.opExtrude","SWEPT_FACE",FACE,{"disambiguationData":[OSD([subQ2,subQ0])]})],"blendedInto":[makeQuery(id+"F1.opExtrude","SWEPT_FACE",FACE,{"disambiguationData":[OSD([subQ2,subQ0])]})]}),makeQuery(id+"F13.opExtrude","CAP_EDGE",EDGE,{"disambiguationData":[OSD([subQ2,subQ1,subQ0])],"isStart":true})]});}
            fillet(context, id + "F15", {"entities" : qUnion([Q0, Q1]), "radius" : 5 * mm, "tangentPropagation" : true, "allowEdgeOverflow" : false});
        }
        {
            var Q0;
            Q0=makeQuery(id+"F13.opExtrude","CAP_EDGE",EDGE,{"disambiguationData":[OSD([sQuery(id+"F0.wireOp",EDGE,"E7.bottom"),sQuery(id+"F0.wireOp",EDGE,"E7.right")])],"isStart":false});
            var Q1;
            Q1=makeQuery(id+"F14.opExtrude","CAP_EDGE",EDGE,{"disambiguationData":[OSD([sQuery(id+"F0.wireOp",EDGE,"E6.bottom"),sQuery(id+"F0.wireOp",EDGE,"E6.right")])],"isStart":false});
            var Q2;
            {var subQ0=sQuery(id+"F0.wireOp",EDGE,"E7.bottom");var subQ1=sQuery(id+"F0.wireOp",EDGE,"E4.top");var subQ2=sQuery(id+"F0.wireOp",EDGE,"E4.right");Q2=makeQuery(id+"F15.opFillet","BLEND_EDGE",EDGE,{"blendedFrom":[makeQuery(id+"F13.boolean.opBoolean","MERGE",EDGE,{"derivedFrom":[makeQuery(id+"F6.opFillet","BLEND_EDGE",EDGE,{"blendedFrom":[makeQuery(id+"F1.opExtrude","SWEPT_EDGE",EDGE,{"disambiguationData":[OSD([subQ1,subQ2])]}),makeQuery(id+"F1.opExtrude","SWEPT_FACE",FACE,{"disambiguationData":[OSD([subQ1,subQ0])]})],"blendedInto":[makeQuery(id+"F1.opExtrude","SWEPT_FACE",FACE,{"disambiguationData":[OSD([subQ1,subQ0])]})]}),makeQuery(id+"F13.opExtrude","CAP_EDGE",EDGE,{"disambiguationData":[OSD([subQ1,subQ2,subQ0])],"isStart":true})]}),makeQuery(id+"F13.opExtrude","CAP_FACE",FACE,{"disambiguationData":[OSD([subQ1,subQ0])],"isStart":false})],"blendedInto":[makeQuery(id+"F13.opExtrude","CAP_FACE",FACE,{"disambiguationData":[OSD([subQ1,subQ0])],"isStart":false})]});}
            var Q3;
            {var subQ0=sQuery(id+"F0.wireOp",EDGE,"E6.bottom");var subQ1=sQuery(id+"F0.wireOp",EDGE,"E4.bottom");var subQ2=sQuery(id+"F0.wireOp",EDGE,"E4.right");Q3=makeQuery(id+"F15.opFillet","BLEND_EDGE",EDGE,{"blendedFrom":[makeQuery(id+"F14.boolean.opBoolean","MERGE",EDGE,{"derivedFrom":[makeQuery(id+"F6.opFillet","BLEND_EDGE",EDGE,{"blendedFrom":[makeQuery(id+"F1.opExtrude","SWEPT_EDGE",EDGE,{"disambiguationData":[OSD([subQ1,subQ2])]}),makeQuery(id+"F1.opExtrude","SWEPT_FACE",FACE,{"disambiguationData":[OSD([subQ1,subQ0])]})],"blendedInto":[makeQuery(id+"F1.opExtrude","SWEPT_FACE",FACE,{"disambiguationData":[OSD([subQ1,subQ0])]})]}),makeQuery(id+"F14.opExtrude","CAP_EDGE",EDGE,{"disambiguationData":[OSD([subQ1,subQ2,subQ0])],"isStart":true})]}),makeQuery(id+"F14.opExtrude","CAP_FACE",FACE,{"disambiguationData":[OSD([subQ1,subQ0])],"isStart":false})],"blendedInto":[makeQuery(id+"F14.opExtrude","CAP_FACE",FACE,{"disambiguationData":[OSD([subQ1,subQ0])],"isStart":false})]});}
            fillet(context, id + "F16", {"entities" : qUnion([Q0, Q1, Q2, Q3]), "radius" : 1 * mm, "tangentPropagation" : true, "allowEdgeOverflow" : false});
        }
    });
